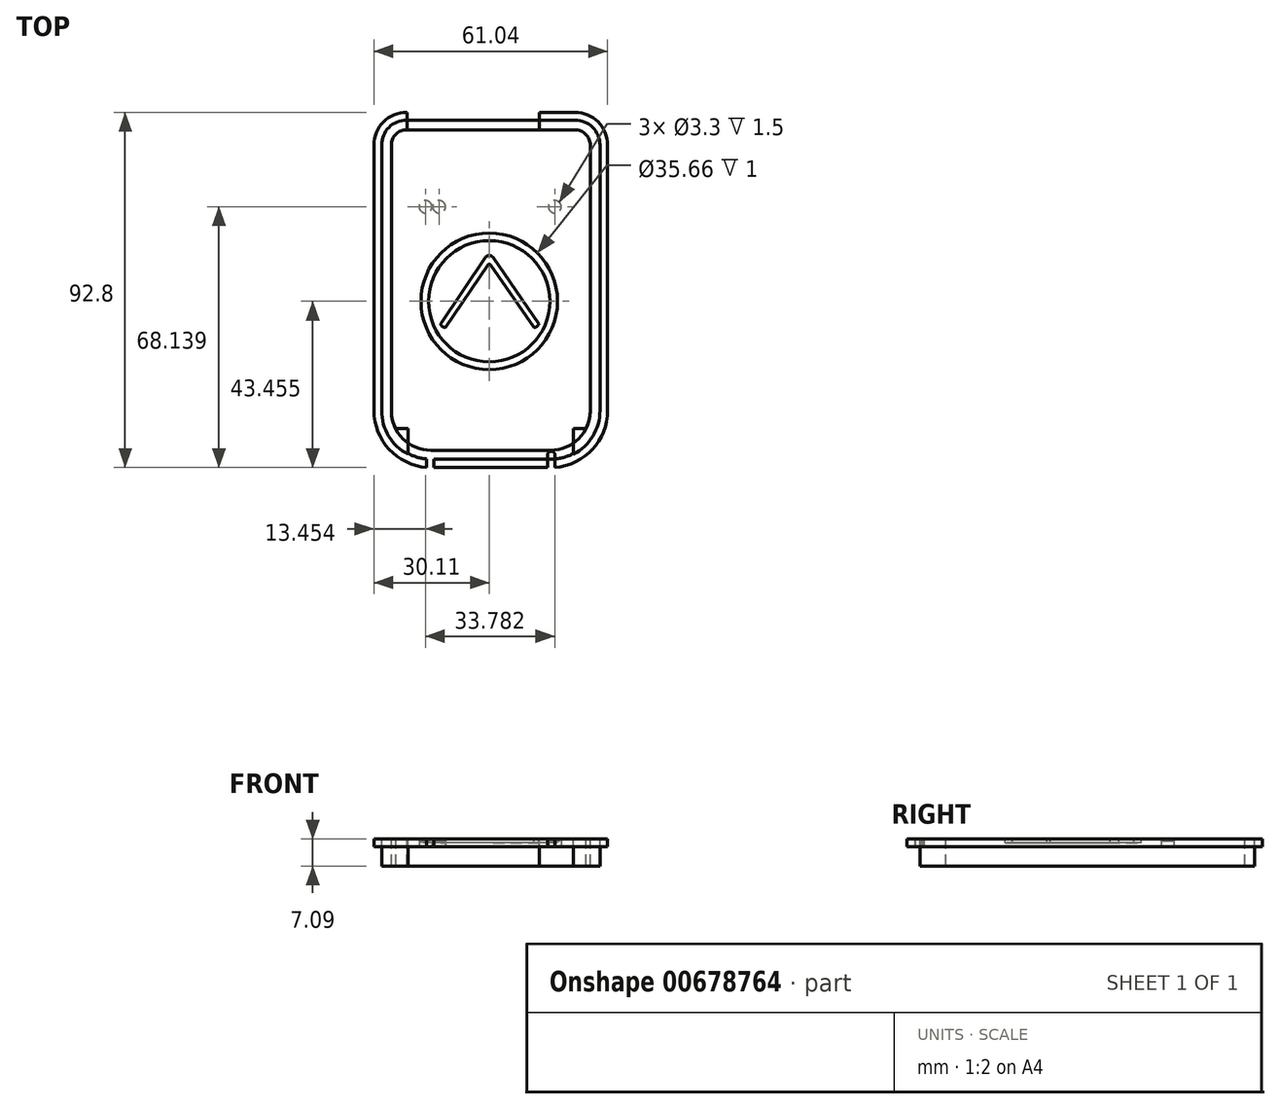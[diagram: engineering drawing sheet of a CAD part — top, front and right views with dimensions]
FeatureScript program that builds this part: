
annotation { "Feature Type Name" : "Feature", "Feature Type Description" : "" }
export const myFeature = defineFeature(function(context is Context, id is Id, definition is map)
    precondition{}
    {
        {
            var Q0;
            Q0=qCreatedBy(makeId("Top.planeOp"),FACE);
            var sketch = newSketch(context, id + "F0", { "sketchPlane" : qUnion([Q0])});
            skLineSegment(sketch, "E0.bottom", {"start": v(21.97, 44.2) * mm, "end": v(-21.97, 44.2) * mm});
            skLineSegment(sketch, "E0.top", {"start": v(15.62, -44.2) * mm, "end": v(-15.62, -44.2) * mm});
            skLineSegment(sketch, "E0.left", {"start": v(28.32, 37.85) * mm, "end": v(28.32, -31.5) * mm});
            skLineSegment(sketch, "E0.right", {"start": v(-28.32, 37.85) * mm, "end": v(-28.32, -31.5) * mm});
            skPoint(sketch, "E1.visualSharp", {"position": v(-28.32, 44.2) * mm});
            skArc(sketch, "E1.filletArc", {"start": v(-21.97, 44.2) * mm, "mid": v(-26.46, 42.34) * mm, "end": v(-28.32, 37.85) * mm});
            skPoint(sketch, "E2.visualSharp", {"position": v(28.32, 44.2) * mm});
            skArc(sketch, "E2.filletArc", {"start": v(28.32, 37.85) * mm, "mid": v(26.46, 42.34) * mm, "end": v(21.97, 44.2) * mm});
            skPoint(sketch, "E3.visualSharp", {"position": v(-28.32, -44.2) * mm});
            skArc(sketch, "E3.filletArc", {"start": v(-28.32, -31.5) * mm, "mid": v(-24.6, -40.48) * mm, "end": v(-15.62, -44.2) * mm});
            skPoint(sketch, "E4.visualSharp", {"position": v(28.32, -44.2) * mm});
            skArc(sketch, "E4.filletArc", {"start": v(15.62, -44.2) * mm, "mid": v(24.6, -40.48) * mm, "end": v(28.32, -31.5) * mm});
            skLineSegment(sketch, "E5.0", {"start": v(21.97, 44.4) * mm, "end": v(-21.97, 44.4) * mm});
            skArc(sketch, "E5.1", {"start": v(28.52, 37.85) * mm, "mid": v(26.6, 42.48) * mm, "end": v(21.97, 44.4) * mm});
            skArc(sketch, "E5.2", {"start": v(-21.97, 44.4) * mm, "mid": v(-26.6, 42.48) * mm, "end": v(-28.52, 37.85) * mm});
            skLineSegment(sketch, "E5.3", {"start": v(28.52, 37.85) * mm, "end": v(28.52, -31.5) * mm});
            skLineSegment(sketch, "E5.4", {"start": v(-28.52, 37.85) * mm, "end": v(-28.52, -31.5) * mm});
            skArc(sketch, "E5.5", {"start": v(-28.52, -31.5) * mm, "mid": v(-24.74, -40.62) * mm, "end": v(-15.62, -44.4) * mm});
            skLineSegment(sketch, "E5.6", {"start": v(15.62, -44.4) * mm, "end": v(-15.62, -44.4) * mm});
            skArc(sketch, "E5.7", {"start": v(15.62, -44.4) * mm, "mid": v(24.74, -40.62) * mm, "end": v(28.52, -31.5) * mm});
            skArc(sketch, "E6.0", {"start": v(-21.97, 46.4) * mm, "mid": v(-28.02, 43.9) * mm, "end": v(-30.52, 37.85) * mm});
            skLineSegment(sketch, "E6.1", {"start": v(21.97, 46.4) * mm, "end": v(-21.97, 46.4) * mm});
            skLineSegment(sketch, "E6.2", {"start": v(-30.52, 37.85) * mm, "end": v(-30.52, -31.5) * mm});
            skArc(sketch, "E6.3", {"start": v(30.52, 37.85) * mm, "mid": v(28.02, 43.9) * mm, "end": v(21.97, 46.4) * mm});
            skArc(sketch, "E6.4", {"start": v(-30.52, -31.5) * mm, "mid": v(-26.16, -42.03) * mm, "end": v(-15.62, -46.4) * mm});
            skLineSegment(sketch, "E6.5", {"start": v(15.62, -46.4) * mm, "end": v(-15.62, -46.4) * mm});
            skArc(sketch, "E6.6", {"start": v(15.62, -46.4) * mm, "mid": v(26.16, -42.03) * mm, "end": v(30.52, -31.5) * mm});
            skLineSegment(sketch, "E6.7", {"start": v(30.52, 37.85) * mm, "end": v(30.52, -31.5) * mm});
            skArc(sketch, "E7.0", {"start": v(25.98, 37.85) * mm, "mid": v(24.8, 40.68) * mm, "end": v(21.97, 41.86) * mm});
            skLineSegment(sketch, "E7.1", {"start": v(25.98, 37.85) * mm, "end": v(25.98, -31.5) * mm});
            skLineSegment(sketch, "E7.2", {"start": v(21.97, 41.86) * mm, "end": v(-21.97, 41.86) * mm});
            skArc(sketch, "E7.3", {"start": v(15.62, -41.86) * mm, "mid": v(22.95, -38.82) * mm, "end": v(25.98, -31.5) * mm});
            skArc(sketch, "E7.4", {"start": v(-21.97, 41.86) * mm, "mid": v(-24.8, 40.68) * mm, "end": v(-25.98, 37.85) * mm});
            skLineSegment(sketch, "E7.5", {"start": v(-25.98, 37.85) * mm, "end": v(-25.98, -31.5) * mm});
            skArc(sketch, "E7.6", {"start": v(-25.98, -31.5) * mm, "mid": v(-22.95, -38.82) * mm, "end": v(-15.62, -41.86) * mm});
            skLineSegment(sketch, "E7.7", {"start": v(15.62, -41.86) * mm, "end": v(-15.62, -41.86) * mm});
            skLineSegment(sketch, "E8", {"start": v(25.98, -39.18) * mm, "end": v(25.98, -31.5) * mm});
            skLineSegment(sketch, "E9", {"start": v(-25.98, -31.5) * mm, "end": v(-25.98, -39.18) * mm});
            skLineSegment(sketch, "E10", {"start": v(-20.97, -45.4) * mm, "end": v(-20.97, -43.23) * mm});
            skLineSegment(sketch, "E11", {"start": v(21.45, -45.2) * mm, "end": v(21.45, -43) * mm});
            skLineSegment(sketch, "E12.bottom", {"start": v(12.65, 46.4) * mm, "end": v(-21.9, 46.4) * mm});
            skLineSegment(sketch, "E12.right", {"start": v(-21.9, 46.4) * mm, "end": v(-21.9, 42.4) * mm});
            skLineSegment(sketch, "E13", {"start": v(-21.9, 46.4) * mm, "end": v(-21.9, 41.86) * mm});
            skLineSegment(sketch, "E14", {"start": v(12.65, 46.4) * mm, "end": v(12.65, 41.86) * mm});
            skLineSegment(sketch, "E15", {"start": v(15.79, -43.1) * mm, "end": v(15.79, -46.4) * mm});
            skLineSegment(sketch, "E16", {"start": v(-15.79, -43.1) * mm, "end": v(-15.79, -46.4) * mm});
            skArc(sketch, "E17.0.startCap", {"start": v(-16.74, -43.1) * mm, "mid": v(-15.79, -42.14) * mm, "end": v(-14.84, -43.1) * mm});
            skLineSegment(sketch, "E17.0.left", {"start": v(-14.84, -43.1) * mm, "end": v(-14.84, -48.17) * mm});
            skLineSegment(sketch, "E17.0.right", {"start": v(-16.74, -43.1) * mm, "end": v(-16.74, -48.17) * mm});
            skArc(sketch, "E18.0.startCap", {"start": v(14.84, -43.1) * mm, "mid": v(15.79, -42.14) * mm, "end": v(16.74, -43.1) * mm});
            skLineSegment(sketch, "E18.0.left", {"start": v(16.74, -43.1) * mm, "end": v(16.74, -48.17) * mm});
            skLineSegment(sketch, "E18.0.right", {"start": v(14.84, -43.1) * mm, "end": v(14.84, -48.17) * mm});
            skLineSegment(sketch, "E19", {"start": v(-21.63, -45.13) * mm, "end": v(-21.63, -36.24) * mm});
            skLineSegment(sketch, "E20", {"start": v(-21.63, -36.24) * mm, "end": v(-29.75, -36.24) * mm});
            skLineSegment(sketch, "E21", {"start": v(21.63, -45.13) * mm, "end": v(21.63, -36.24) * mm});
            skLineSegment(sketch, "E22", {"start": v(21.63, -36.24) * mm, "end": v(29.75, -36.24) * mm});
            skLineSegment(sketch, "E23", {"start": v(25.98, 33.86) * mm, "end": v(28.52, 33.86) * mm});
            skLineSegment(sketch, "E24.0", {"start": v(25.98, 29.54) * mm, "end": v(28.52, 29.54) * mm});
            skSolve(sketch);
        }
        {
            var Q0;
            {var subQ5=sQuery(id+"F0.wireOp",EDGE,"E12.bottom");Q0=makeQuery(id+"F0.imprint","IMPRINT",FACE,{"disambiguationData":[TD([[makeQuery(id+"F0.imprint","IMPRINT",EDGE,{"derivedFrom":subQ5}),1.0]])]});}
            var Q1;
            {var subQ0=sQuery(id+"F0.wireOp",EDGE,"E13");var subQ3=makeQuery(id+"F0.imprint","IMPRINT",VERTEX,{"derivedFrom":subQ0});Q1=makeQuery(id+"F0.imprint","IMPRINT",FACE,{"disambiguationData":[TD([[makeQuery(id+"F0.imprint","IMPRINT",EDGE,{"disambiguationData":[TD([[subQ3,1.0]])],"derivedFrom":subQ0}),1.0]])]});}
            var Q2;
            {var subQ0=sQuery(id+"F0.wireOp",EDGE,"E14");var subQ1=sQuery(id+"F0.wireOp",EDGE,"E0.bottom");var subQ2=makeQuery(id+"F0.imprint","INTERSECT",VERTEX,{"derivedFrom":[subQ1,subQ0]});Q2=makeQuery(id+"F0.imprint","IMPRINT",FACE,{"disambiguationData":[TD([[makeQuery(id+"F0.imprint","IMPRINT",EDGE,{"disambiguationData":[TD([[subQ2,-1.0]])],"derivedFrom":subQ1}),-1.0]])]});}
            extrude(context, id + "F1", {"entities" : qUnion([Q0, Q1, Q2]), "oppositeDirection" : true, "depth" : 7.1 * mm, "offsetDistance" : 25.4 * mm});
        }
        {
            var Q0;
            {var subQ4=sQuery(id+"F0.wireOp",EDGE,"E5.1");Q0=makeQuery(id+"F0.imprint","IMPRINT",FACE,{"disambiguationData":[TD([[makeQuery(id+"F0.imprint","IMPRINT",EDGE,{"derivedFrom":subQ4}),-1.0]])]});}
            var Q1;
            {var subQ0=sQuery(id+"F0.wireOp",EDGE,"E11");Q1=makeQuery(id+"F0.imprint","IMPRINT",FACE,{"disambiguationData":[TD([[makeQuery(id+"F0.imprint","IMPRINT",EDGE,{"derivedFrom":subQ0}),1.0]])]});}
            var Q2;
            {var subQ15=sQuery(id+"F0.wireOp",EDGE,"E7.0");Q2=makeQuery(id+"F0.imprint","IMPRINT",FACE,{"disambiguationData":[TD([[makeQuery(id+"F0.imprint","IMPRINT",EDGE,{"derivedFrom":subQ15}),1.0]])]});}
            var Q3;
            {var subQ0=sQuery(id+"F0.wireOp",EDGE,"E18.0.right");var subQ1=sQuery(id+"F0.wireOp",EDGE,"E5.6");var subQ2=makeQuery(id+"F0.imprint","INTERSECT",VERTEX,{"derivedFrom":[subQ1,subQ0]});Q3=makeQuery(id+"F0.imprint","IMPRINT",FACE,{"disambiguationData":[TD([[makeQuery(id+"F0.imprint","IMPRINT",EDGE,{"disambiguationData":[TD([[subQ2,-1.0]])],"derivedFrom":subQ1}),1.0]])]});}
            var Q4;
            {var subQ1=sQuery(id+"F0.wireOp",EDGE,"E5.2");Q4=makeQuery(id+"F0.imprint","IMPRINT",FACE,{"disambiguationData":[TD([[makeQuery(id+"F0.imprint","IMPRINT",EDGE,{"derivedFrom":subQ1}),-1.0]])]});}
            var Q5;
            {var subQ0=sQuery(id+"F0.wireOp",EDGE,"E18.0.right");var subQ1=sQuery(id+"F0.wireOp",EDGE,"E0.top");var subQ2=makeQuery(id+"F0.imprint","INTERSECT",VERTEX,{"derivedFrom":[subQ1,subQ0]});Q5=makeQuery(id+"F0.imprint","IMPRINT",FACE,{"disambiguationData":[TD([[makeQuery(id+"F0.imprint","IMPRINT",EDGE,{"disambiguationData":[TD([[subQ2,-1.0]])],"derivedFrom":subQ1}),1.0]])]});}
            var Q6;
            {var subQ0=sQuery(id+"F0.wireOp",EDGE,"E10");Q6=makeQuery(id+"F0.imprint","IMPRINT",FACE,{"disambiguationData":[TD([[makeQuery(id+"F0.imprint","IMPRINT",EDGE,{"derivedFrom":subQ0}),-1.0]])]});}
            var Q7;
            {var subQ4=sQuery(id+"F0.wireOp",EDGE,"E18.0.left");var subQ5=sQuery(id+"F0.wireOp",EDGE,"E4.filletArc");var subQ6=makeQuery(id+"F0.imprint","INTERSECT",VERTEX,{"derivedFrom":[subQ5,subQ4]});Q7=makeQuery(id+"F0.imprint","IMPRINT",FACE,{"disambiguationData":[TD([[makeQuery(id+"F0.imprint","IMPRINT",EDGE,{"disambiguationData":[TD([[subQ6,-1.0]])],"derivedFrom":subQ5}),-1.0]])]});}
            var Q8;
            {var subQ6=sQuery(id+"F0.wireOp",EDGE,"E18.0.startCap");Q8=makeQuery(id+"F0.imprint","IMPRINT",FACE,{"disambiguationData":[TD([[makeQuery(id+"F0.imprint","IMPRINT",EDGE,{"derivedFrom":subQ6}),1.0]])]});}
            var Q9;
            {var subQ3=sQuery(id+"F0.wireOp",EDGE,"E5.7");var subQ7=makeQuery(id+"F0.imprint","INTERSECT",VERTEX,{"derivedFrom":[subQ3,sQuery(id+"F0.wireOp",EDGE,"E8")]});Q9=makeQuery(id+"F0.imprint","IMPRINT",FACE,{"disambiguationData":[TD([[makeQuery(id+"F0.imprint","IMPRINT",EDGE,{"disambiguationData":[TD([[subQ7,1.0]])],"derivedFrom":subQ3}),-1.0]])]});}
            var Q10;
            {var subQ0=sQuery(id+"F0.wireOp",EDGE,"E21");var subQ1=sQuery(id+"F0.wireOp",EDGE,"E7.3");var subQ2=makeQuery(id+"F0.imprint","INTERSECT",VERTEX,{"derivedFrom":[subQ1,subQ0]});Q10=makeQuery(id+"F0.imprint","IMPRINT",FACE,{"disambiguationData":[TD([[makeQuery(id+"F0.imprint","IMPRINT",EDGE,{"disambiguationData":[TD([[subQ2,-1.0]])],"derivedFrom":subQ1}),1.0]])]});}
            var Q11;
            {var subQ0=sQuery(id+"F0.wireOp",EDGE,"E20");var subQ1=sQuery(id+"F0.wireOp",EDGE,"E7.6");var subQ2=makeQuery(id+"F0.imprint","INTERSECT",VERTEX,{"derivedFrom":[subQ1,subQ0]});Q11=makeQuery(id+"F0.imprint","IMPRINT",FACE,{"disambiguationData":[TD([[makeQuery(id+"F0.imprint","IMPRINT",EDGE,{"disambiguationData":[TD([[subQ2,-1.0]])],"derivedFrom":subQ1}),1.0]])]});}
            var Q12;
            {var subQ5=sQuery(id+"F0.wireOp",EDGE,"E5.5");var subQ6=makeQuery(id+"F0.imprint","INTERSECT",VERTEX,{"derivedFrom":[subQ5,sQuery(id+"F0.wireOp",EDGE,"E9")]});Q12=makeQuery(id+"F0.imprint","IMPRINT",FACE,{"disambiguationData":[TD([[makeQuery(id+"F0.imprint","IMPRINT",EDGE,{"disambiguationData":[TD([[subQ6,1.0]])],"derivedFrom":subQ5}),-1.0]])]});}
            var Q13;
            {var subQ0=sQuery(id+"F0.wireOp",EDGE,"E10");Q13=makeQuery(id+"F0.imprint","IMPRINT",FACE,{"disambiguationData":[TD([[makeQuery(id+"F0.imprint","IMPRINT",EDGE,{"derivedFrom":subQ0}),1.0]])]});}
            var Q14;
            {var subQ0=sQuery(id+"F0.wireOp",EDGE,"E11");Q14=makeQuery(id+"F0.imprint","IMPRINT",FACE,{"disambiguationData":[TD([[makeQuery(id+"F0.imprint","IMPRINT",EDGE,{"derivedFrom":subQ0}),-1.0]])]});}
            var Q15;
            {var subQ1=sQuery(id+"F0.wireOp",EDGE,"E3.filletArc");var subQ6=sQuery(id+"F0.wireOp",EDGE,"E19");var subQ8=makeQuery(id+"F0.imprint","INTERSECT",VERTEX,{"derivedFrom":[subQ1,subQ6]});Q15=makeQuery(id+"F0.imprint","IMPRINT",FACE,{"disambiguationData":[TD([[makeQuery(id+"F0.imprint","IMPRINT",EDGE,{"disambiguationData":[TD([[subQ8,-1.0]])],"derivedFrom":subQ1}),-1.0]])]});}
            extrude(context, id + "F2", {"entities" : qUnion([Q0, Q1, Q2, Q3, Q4, Q5, Q6, Q7, Q8, Q9, Q10, Q11, Q12, Q13, Q14, Q15]), "oppositeDirection" : true, "depth" : 2 * mm, "offsetDistance" : 25.4 * mm});
        }
        {
            var Q0;
            {var subQ1=sQuery(id+"F0.wireOp",EDGE,"E0.right");Q0=makeQuery(id+"F0.imprint","IMPRINT",FACE,{"disambiguationData":[TD([[makeQuery(id+"F0.imprint","IMPRINT",EDGE,{"derivedFrom":subQ1}),1.0]])]});}
            var Q1;
            {var subQ1=sQuery(id+"F0.wireOp",EDGE,"E0.left");Q1=makeQuery(id+"F0.imprint","IMPRINT",FACE,{"disambiguationData":[TD([[makeQuery(id+"F0.imprint","IMPRINT",EDGE,{"derivedFrom":subQ1}),-1.0]])]});}
            var Q2;
            {var subQ1=sQuery(id+"F0.wireOp",EDGE,"E0.left");Q2=makeQuery(id+"F0.imprint","IMPRINT",FACE,{"disambiguationData":[TD([[makeQuery(id+"F0.imprint","IMPRINT",EDGE,{"derivedFrom":subQ1}),1.0]])]});}
            var Q3;
            {var subQ1=sQuery(id+"F0.wireOp",EDGE,"E0.right");Q3=makeQuery(id+"F0.imprint","IMPRINT",FACE,{"disambiguationData":[TD([[makeQuery(id+"F0.imprint","IMPRINT",EDGE,{"derivedFrom":subQ1}),-1.0]])]});}
            var Q4;
            {var subQ1=sQuery(id+"F0.wireOp",EDGE,"E7.6");var subQ3=sQuery(id+"F0.wireOp",EDGE,"E20");var subQ4=makeQuery(id+"F0.imprint","INTERSECT",VERTEX,{"derivedFrom":[subQ1,subQ3]});Q4=makeQuery(id+"F0.imprint","IMPRINT",FACE,{"disambiguationData":[TD([[makeQuery(id+"F0.imprint","IMPRINT",EDGE,{"disambiguationData":[TD([[subQ4,-1.0]])],"derivedFrom":subQ3}),-1.0]])]});}
            var Q5;
            {var subQ0=sQuery(id+"F0.wireOp",EDGE,"E20");var subQ1=sQuery(id+"F0.wireOp",EDGE,"E3.filletArc");var subQ2=makeQuery(id+"F0.imprint","INTERSECT",VERTEX,{"derivedFrom":[subQ1,subQ0]});Q5=makeQuery(id+"F0.imprint","IMPRINT",FACE,{"disambiguationData":[TD([[makeQuery(id+"F0.imprint","IMPRINT",EDGE,{"disambiguationData":[TD([[subQ2,-1.0]])],"derivedFrom":subQ1}),1.0]])]});}
            var Q6;
            {var subQ0=sQuery(id+"F0.wireOp",EDGE,"E9");var subQ1=sQuery(id+"F0.wireOp",EDGE,"E3.filletArc");var subQ2=makeQuery(id+"F0.imprint","INTERSECT",VERTEX,{"derivedFrom":[subQ1,subQ0]});Q6=makeQuery(id+"F0.imprint","IMPRINT",FACE,{"disambiguationData":[TD([[makeQuery(id+"F0.imprint","IMPRINT",EDGE,{"disambiguationData":[TD([[subQ2,-1.0]])],"derivedFrom":subQ1}),1.0]])]});}
            var Q7;
            {var subQ0=sQuery(id+"F0.wireOp",EDGE,"E20");var subQ1=sQuery(id+"F0.wireOp",EDGE,"E7.6");var subQ2=makeQuery(id+"F0.imprint","INTERSECT",VERTEX,{"derivedFrom":[subQ1,subQ0]});Q7=makeQuery(id+"F0.imprint","IMPRINT",FACE,{"disambiguationData":[TD([[makeQuery(id+"F0.imprint","IMPRINT",EDGE,{"disambiguationData":[TD([[subQ2,-1.0]])],"derivedFrom":subQ1}),1.0]])]});}
            var Q8;
            {var subQ0=sQuery(id+"F0.wireOp",EDGE,"E20");var subQ1=sQuery(id+"F0.wireOp",EDGE,"E3.filletArc");var subQ2=makeQuery(id+"F0.imprint","INTERSECT",VERTEX,{"derivedFrom":[subQ1,subQ0]});Q8=makeQuery(id+"F0.imprint","IMPRINT",FACE,{"disambiguationData":[TD([[makeQuery(id+"F0.imprint","IMPRINT",EDGE,{"disambiguationData":[TD([[subQ2,-1.0]])],"derivedFrom":subQ1}),-1.0]])]});}
            var Q9;
            {var subQ0=sQuery(id+"F0.wireOp",EDGE,"E9");var subQ1=sQuery(id+"F0.wireOp",EDGE,"E3.filletArc");var subQ2=makeQuery(id+"F0.imprint","INTERSECT",VERTEX,{"derivedFrom":[subQ1,subQ0]});Q9=makeQuery(id+"F0.imprint","IMPRINT",FACE,{"disambiguationData":[TD([[makeQuery(id+"F0.imprint","IMPRINT",EDGE,{"disambiguationData":[TD([[subQ2,-1.0]])],"derivedFrom":subQ1}),-1.0]])]});}
            var Q10;
            {var subQ1=sQuery(id+"F0.wireOp",EDGE,"E7.3");var subQ3=sQuery(id+"F0.wireOp",EDGE,"E22");var subQ4=makeQuery(id+"F0.imprint","INTERSECT",VERTEX,{"derivedFrom":[subQ1,subQ3]});Q10=makeQuery(id+"F0.imprint","IMPRINT",FACE,{"disambiguationData":[TD([[makeQuery(id+"F0.imprint","IMPRINT",EDGE,{"disambiguationData":[TD([[subQ4,-1.0]])],"derivedFrom":subQ3}),1.0]])]});}
            var Q11;
            {var subQ0=sQuery(id+"F0.wireOp",EDGE,"E8");var subQ1=sQuery(id+"F0.wireOp",EDGE,"E4.filletArc");var subQ2=makeQuery(id+"F0.imprint","INTERSECT",VERTEX,{"derivedFrom":[subQ1,subQ0]});Q11=makeQuery(id+"F0.imprint","IMPRINT",FACE,{"disambiguationData":[TD([[makeQuery(id+"F0.imprint","IMPRINT",EDGE,{"disambiguationData":[TD([[subQ2,-1.0]])],"derivedFrom":subQ1}),1.0]])]});}
            var Q12;
            {var subQ0=sQuery(id+"F0.wireOp",EDGE,"E21");var subQ1=sQuery(id+"F0.wireOp",EDGE,"E4.filletArc");var subQ2=makeQuery(id+"F0.imprint","INTERSECT",VERTEX,{"derivedFrom":[subQ1,subQ0]});Q12=makeQuery(id+"F0.imprint","IMPRINT",FACE,{"disambiguationData":[TD([[makeQuery(id+"F0.imprint","IMPRINT",EDGE,{"disambiguationData":[TD([[subQ2,-1.0]])],"derivedFrom":subQ1}),1.0]])]});}
            var Q13;
            {var subQ0=sQuery(id+"F0.wireOp",EDGE,"E21");var subQ1=sQuery(id+"F0.wireOp",EDGE,"E4.filletArc");var subQ2=makeQuery(id+"F0.imprint","INTERSECT",VERTEX,{"derivedFrom":[subQ1,subQ0]});Q13=makeQuery(id+"F0.imprint","IMPRINT",FACE,{"disambiguationData":[TD([[makeQuery(id+"F0.imprint","IMPRINT",EDGE,{"disambiguationData":[TD([[subQ2,-1.0]])],"derivedFrom":subQ1}),-1.0]])]});}
            var Q14;
            {var subQ0=sQuery(id+"F0.wireOp",EDGE,"E8");var subQ1=sQuery(id+"F0.wireOp",EDGE,"E4.filletArc");var subQ2=makeQuery(id+"F0.imprint","INTERSECT",VERTEX,{"derivedFrom":[subQ1,subQ0]});Q14=makeQuery(id+"F0.imprint","IMPRINT",FACE,{"disambiguationData":[TD([[makeQuery(id+"F0.imprint","IMPRINT",EDGE,{"disambiguationData":[TD([[subQ2,-1.0]])],"derivedFrom":subQ1}),-1.0]])]});}
            var Q15;
            {var subQ0=sQuery(id+"F0.wireOp",EDGE,"E21");var subQ1=sQuery(id+"F0.wireOp",EDGE,"E7.3");var subQ2=makeQuery(id+"F0.imprint","INTERSECT",VERTEX,{"derivedFrom":[subQ1,subQ0]});Q15=makeQuery(id+"F0.imprint","IMPRINT",FACE,{"disambiguationData":[TD([[makeQuery(id+"F0.imprint","IMPRINT",EDGE,{"disambiguationData":[TD([[subQ2,-1.0]])],"derivedFrom":subQ1}),1.0]])]});}
            var Q16;
            {var subQ7=sQuery(id+"F0.wireOp",EDGE,"E4.filletArc");var subQ8=sQuery(id+"F0.wireOp",EDGE,"E0.left");var subQ9=makeQuery(id+"F0.imprint","INTERSECT",VERTEX,{"derivedFrom":[subQ8,subQ7]});Q16=makeQuery(id+"F0.imprint","IMPRINT",FACE,{"disambiguationData":[TD([[makeQuery(id+"F0.imprint","IMPRINT",EDGE,{"disambiguationData":[TD([[subQ9,1.0]])],"derivedFrom":subQ8}),-1.0]])]});}
            var Q17;
            {var subQ1=sQuery(id+"F0.wireOp",EDGE,"E2.filletArc");Q17=makeQuery(id+"F0.imprint","IMPRINT",FACE,{"disambiguationData":[TD([[makeQuery(id+"F0.imprint","IMPRINT",EDGE,{"derivedFrom":subQ1}),1.0]])]});}
            var Q18;
            {var subQ6=sQuery(id+"F0.wireOp",EDGE,"E2.filletArc");Q18=makeQuery(id+"F0.imprint","IMPRINT",FACE,{"disambiguationData":[TD([[makeQuery(id+"F0.imprint","IMPRINT",EDGE,{"derivedFrom":subQ6}),-1.0]])]});}
            var Q19;
            {var subQ5=sQuery(id+"F0.wireOp",EDGE,"E4.filletArc");var subQ9=sQuery(id+"F0.wireOp",EDGE,"E0.left");var subQ10=makeQuery(id+"F0.imprint","INTERSECT",VERTEX,{"derivedFrom":[subQ9,subQ5]});Q19=makeQuery(id+"F0.imprint","IMPRINT",FACE,{"disambiguationData":[TD([[makeQuery(id+"F0.imprint","IMPRINT",EDGE,{"disambiguationData":[TD([[subQ10,1.0]])],"derivedFrom":subQ9}),1.0]])]});}
            extrude(context, id + "F3", {"entities" : qUnion([Q0, Q1, Q2, Q3, Q4, Q5, Q6, Q7, Q8, Q9, Q10, Q11, Q12, Q13, Q14, Q15, Q16, Q17, Q18, Q19]), "oppositeDirection" : true, "depth" : 7.1 * mm, "offsetDistance" : 25.4 * mm});
        }
        {
            var Q0;
            {var subQ13=sQuery(id+"F0.wireOp",EDGE,"E7.0");Q0=makeQuery(id+"F0.imprint","IMPRINT",FACE,{"disambiguationData":[TD([[makeQuery(id+"F0.imprint","IMPRINT",EDGE,{"derivedFrom":subQ13}),1.0]])]});}
            var sketch = newSketch(context, id + "F4", { "sketchPlane" : qUnion([Q0])});
            skCircle(sketch, "E25", {"center": v(-0.4, -2.95) * mm, "radius": 17.83 * mm});
            skCircle(sketch, "E26", {"center": v(-0.4, -2.95) * mm, "radius": 15.84 * mm});
            skLineSegment(sketch, "E27", {"start": v(-1.37, 8.5) * mm, "end": v(-13.14, -8.87) * mm});
            skLineSegment(sketch, "E28", {"start": v(0.56, 8.5) * mm, "end": v(12.57, -8.87) * mm});
            skLineSegment(sketch, "E29", {"start": v(11.25, -9.78) * mm, "end": v(0, 6.5) * mm});
            skLineSegment(sketch, "E30", {"start": v(-0.82, 6.49) * mm, "end": v(-11.84, -9.78) * mm});
            skPoint(sketch, "E31.visualSharp", {"position": v(-0.4, 9.91) * mm});
            skArc(sketch, "E31.filletArc", {"start": v(0.56, 8.5) * mm, "mid": v(-0.4, 9.01) * mm, "end": v(-1.37, 8.5) * mm});
            skPoint(sketch, "E32.visualSharp", {"position": v(-0.4, 7.1) * mm});
            skArc(sketch, "E32.filletArc", {"start": v(0, 6.5) * mm, "mid": v(-0.4, 6.7) * mm, "end": v(-0.82, 6.49) * mm});
            skArc(sketch, "E33", {"start": v(-13.14, -8.87) * mm, "mid": v(-12.63, -9.52) * mm, "end": v(-11.84, -9.78) * mm});
            skArc(sketch, "E34", {"start": v(11.25, -9.78) * mm, "mid": v(12.05, -9.53) * mm, "end": v(12.57, -8.87) * mm});
            skLineSegment(sketch, "E35.direction1", {"start": v(-17.8, -44.95) * mm, "end": v(-12.8, -44.95) * mm, "construction": true});
            skSolve(sketch);
        }
        {
            var Q0;
            Q0=qSketchRegion(id+"F4",true);
            var Q1;
            Q1=makeQuery(id+"F4.imprint","IMPRINT",FACE,{"disambiguationData":[TD([[makeQuery(id+"F4.imprint","IMPRINT",EDGE,{"derivedFrom":sQuery(id+"F4.wireOp",EDGE,"E27")}),1.0]])]});
            extrude(context, id + "F5", {"entities" : qUnion([Q0, Q1]), "operationType" : NewBodyOperationType.REMOVE, "oppositeDirection" : true, "depth" : 1 * mm, "offsetDistance" : 25.4 * mm});
        }
        {
            var Q0;
            Q0=makeQuery(id+"F2.opExtrude","CAP_FACE",FACE,{"disambiguationData":[OSD([sQuery(id+"F0.wireOp",EDGE,"E5.0"),sQuery(id+"F0.wireOp",EDGE,"E5.1"),sQuery(id+"F0.wireOp",EDGE,"E5.2"),sQuery(id+"F0.wireOp",EDGE,"E5.3"),sQuery(id+"F0.wireOp",EDGE,"E5.4"),sQuery(id+"F0.wireOp",EDGE,"E5.5"),sQuery(id+"F0.wireOp",EDGE,"E5.7"),sQuery(id+"F0.wireOp",EDGE,"E6.0"),sQuery(id+"F0.wireOp",EDGE,"E6.1"),sQuery(id+"F0.wireOp",EDGE,"E6.2"),sQuery(id+"F0.wireOp",EDGE,"E6.3"),sQuery(id+"F0.wireOp",EDGE,"E6.4"),sQuery(id+"F0.wireOp",EDGE,"E6.5"),sQuery(id+"F0.wireOp",EDGE,"E6.6"),sQuery(id+"F0.wireOp",EDGE,"E6.7"),sQuery(id+"F0.wireOp",EDGE,"E7.0"),sQuery(id+"F0.wireOp",EDGE,"E7.1"),sQuery(id+"F0.wireOp",EDGE,"E7.2"),sQuery(id+"F0.wireOp",EDGE,"E7.3"),sQuery(id+"F0.wireOp",EDGE,"E7.4"),sQuery(id+"F0.wireOp",EDGE,"E7.5"),sQuery(id+"F0.wireOp",EDGE,"E7.6"),sQuery(id+"F0.wireOp",EDGE,"E13"),sQuery(id+"F0.wireOp",EDGE,"E14"),sQuery(id+"F0.wireOp",EDGE,"E17.0.startCap"),sQuery(id+"F0.wireOp",EDGE,"E17.0.left"),sQuery(id+"F0.wireOp",EDGE,"E17.0.right"),sQuery(id+"F0.wireOp",EDGE,"E18.0.startCap"),sQuery(id+"F0.wireOp",EDGE,"E18.0.left"),sQuery(id+"F0.wireOp",EDGE,"E18.0.right"),sQuery(id+"F0.wireOp",EDGE,"E19"),sQuery(id+"F0.wireOp",EDGE,"E21")])],"isStart":false});
            var sketch = newSketch(context, id + "F6", { "sketchPlane" : qUnion([Q0])});
            skCircle(sketch, "E36", {"center": v(-17.07, -21.74) * mm, "radius": 1.65 * mm});
            skCircle(sketch, "E37", {"center": v(-13.5, -21.74) * mm, "radius": 1.65 * mm});
            skCircle(sketch, "E38", {"center": v(16.72, -21.74) * mm, "radius": 1.65 * mm});
            skSolve(sketch);
        }
        {
            var Q0;
            Q0=makeQuery(id+"F6.imprint","IMPRINT",FACE,{"disambiguationData":[TD([[makeQuery(id+"F6.imprint","IMPRINT",EDGE,{"derivedFrom":sQuery(id+"F6.wireOp",EDGE,"E36")}),1.0]])]});
            var Q1;
            Q1=makeQuery(id+"F6.imprint","IMPRINT",FACE,{"disambiguationData":[TD([[makeQuery(id+"F6.imprint","IMPRINT",EDGE,{"derivedFrom":sQuery(id+"F6.wireOp",EDGE,"E37")}),1.0]])]});
            var Q2;
            Q2=makeQuery(id+"F6.imprint","IMPRINT",FACE,{"disambiguationData":[TD([[makeQuery(id+"F6.imprint","IMPRINT",EDGE,{"derivedFrom":sQuery(id+"F6.wireOp",EDGE,"E38")}),1.0]])]});
            extrude(context, id + "F7", {"entities" : qUnion([Q0, Q1, Q2]), "operationType" : NewBodyOperationType.REMOVE, "oppositeDirection" : true, "depth" : 1.5 * mm, "offsetDistance" : 25.4 * mm});
        }
    });
